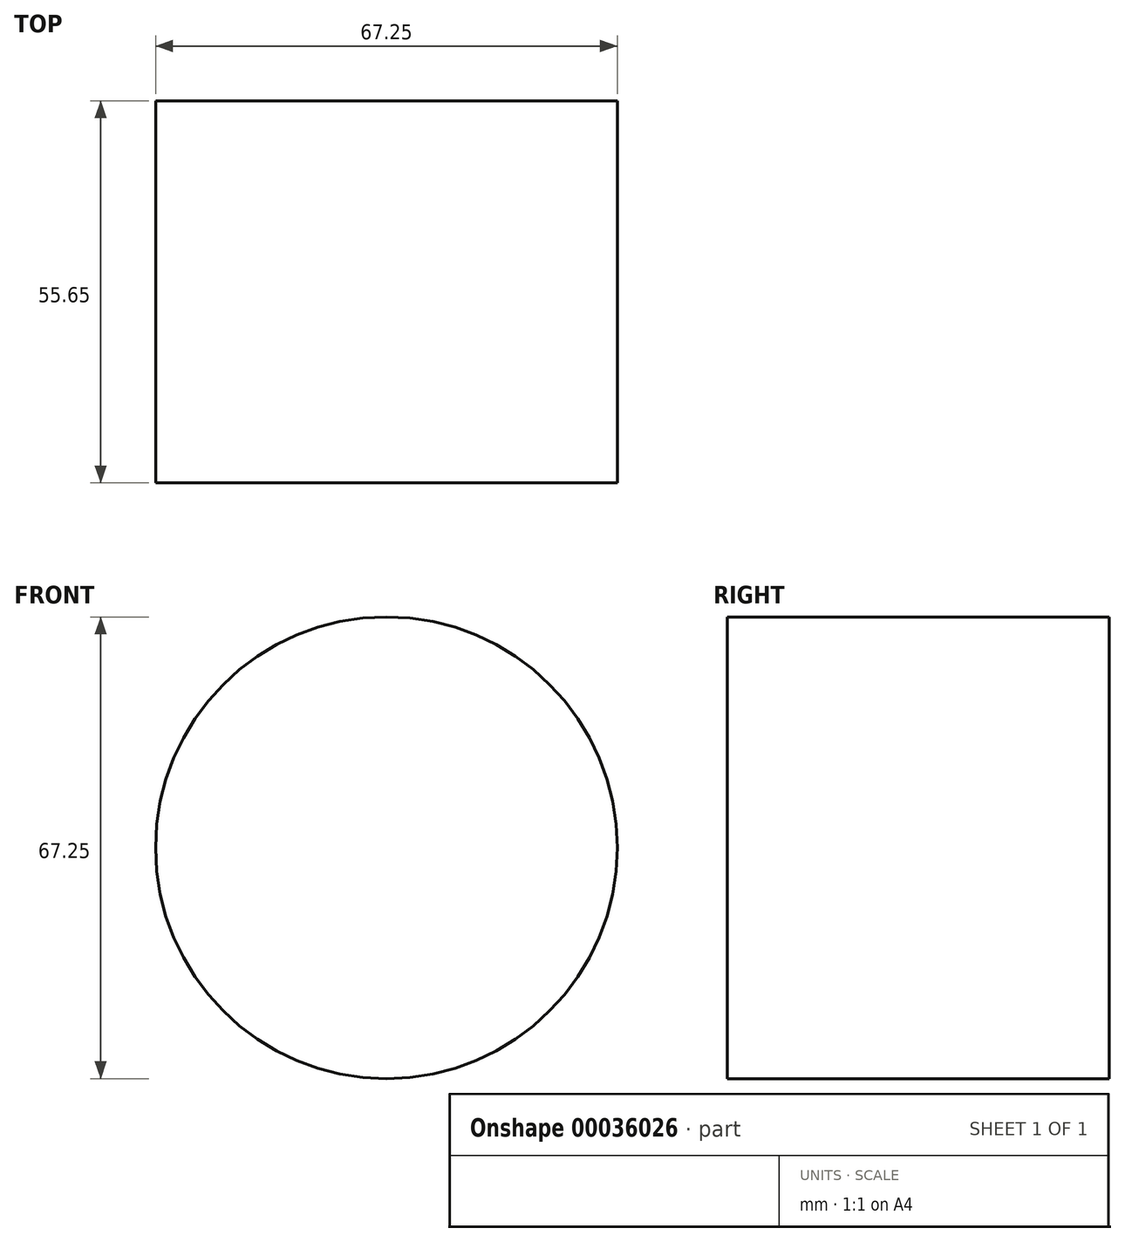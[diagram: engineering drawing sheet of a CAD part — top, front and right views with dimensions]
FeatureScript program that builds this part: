
annotation { "Feature Type Name" : "Feature", "Feature Type Description" : "" }
export const myFeature = defineFeature(function(context is Context, id is Id, definition is map)
    precondition{}
    {
        {
            var Q0;
            Q0=qCreatedBy(makeId("Front.planeOp"),FACE);
            var sketch = newSketch(context, id + "F0", { "sketchPlane" : qUnion([Q0])});
            skCircle(sketch, "E0", {"center": v(-6.97, 9.73) * mm, "radius": 33.62 * mm});
            skSolve(sketch);
        }
        {
            var Q0;
            Q0=makeQuery(id+"F0.imprint","IMPRINT",FACE,{"disambiguationData":[TD([[makeQuery(id+"F0.imprint","IMPRINT",EDGE,{"derivedFrom":sQuery(id+"F0.wireOp",EDGE,"E0")}),1.0]])]});
            extrude(context, id + "F1", {"entities" : qUnion([Q0]), "oppositeDirection" : true, "depth" : 55.65 * mm});
        }
    });
